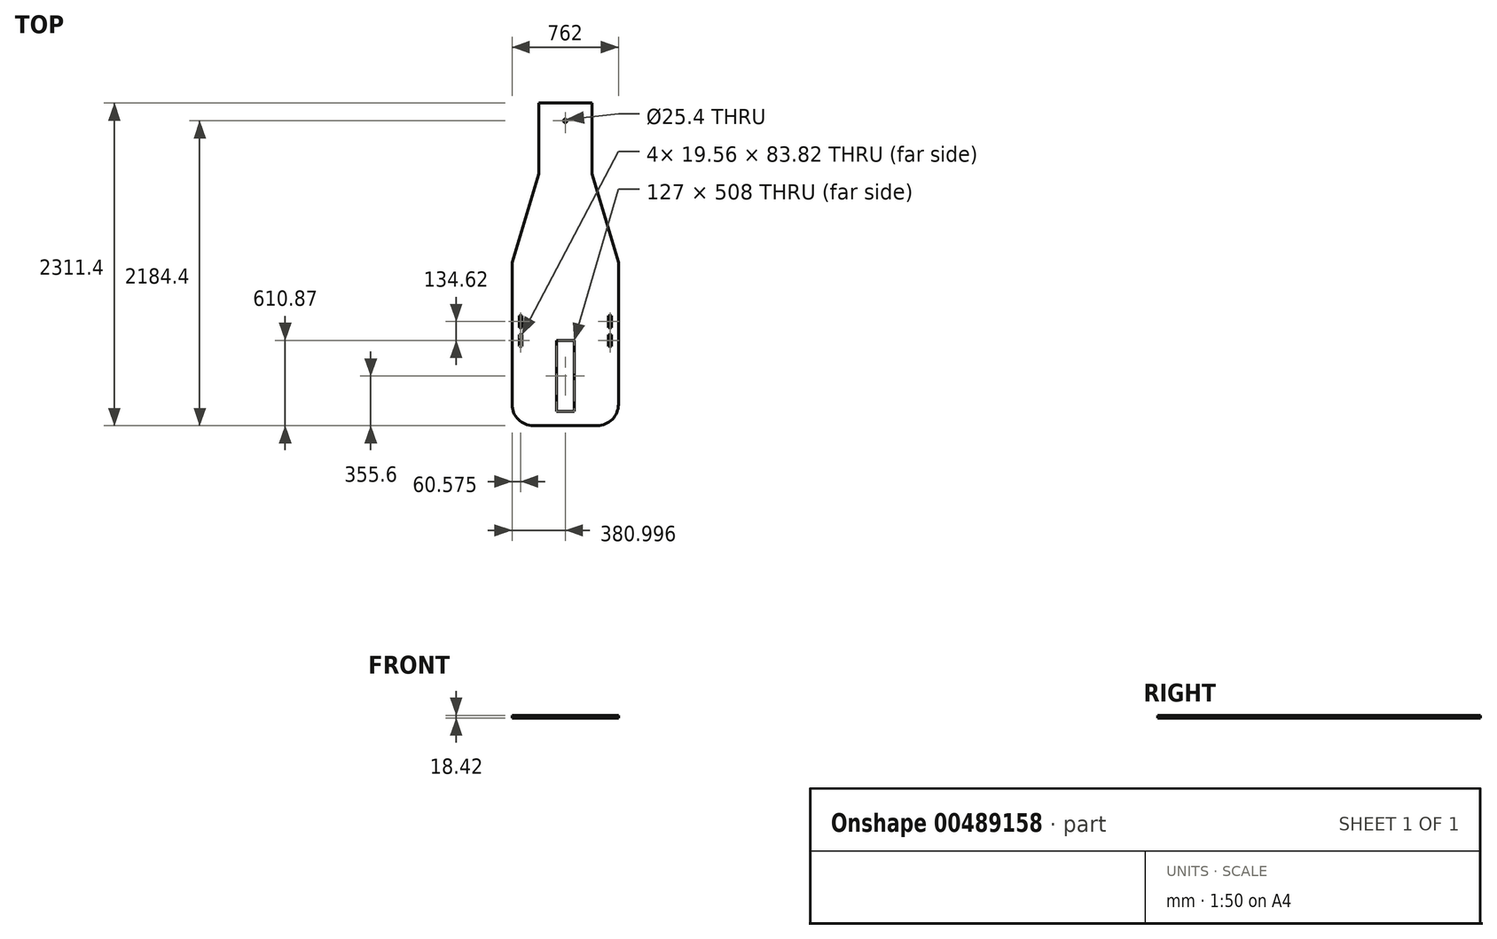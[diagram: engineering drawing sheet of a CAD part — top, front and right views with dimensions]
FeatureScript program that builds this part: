
annotation { "Feature Type Name" : "Feature", "Feature Type Description" : "" }
export const myFeature = defineFeature(function(context is Context, id is Id, definition is map)
    precondition{}
    {
        {
            var Q0;
            Q0=qCreatedBy(makeId("Top.planeOp"),FACE);
            var sketch = newSketch(context, id + "F0", { "sketchPlane" : qUnion([Q0])});
            skLineSegment(sketch, "E0.bottom", {"start": v(158.39, 0) * mm, "end": v(615.59, 0) * mm});
            skLineSegment(sketch, "E1.bottom", {"start": v(323.49, 609.6) * mm, "end": v(450.49, 609.6) * mm});
            skLineSegment(sketch, "E1.top", {"start": v(323.49, 101.6) * mm, "end": v(450.49, 101.6) * mm});
            skLineSegment(sketch, "E1.left", {"start": v(323.49, 609.6) * mm, "end": v(323.49, 101.6) * mm});
            skLineSegment(sketch, "E1.right", {"start": v(450.49, 609.6) * mm, "end": v(450.49, 101.6) * mm});
            skPoint(sketch, "E2.visualSharp", {"position": v(0, 0) * mm});
            skArc(sketch, "E2.filletArc", {"start": v(5.99, 152.4) * mm, "mid": v(50.62, 44.64) * mm, "end": v(158.39, 0) * mm});
            skPoint(sketch, "E3.visualSharp", {"position": v(762, 0) * mm});
            skArc(sketch, "E3.filletArc", {"start": v(615.59, 0) * mm, "mid": v(723.35, 44.64) * mm, "end": v(767.99, 152.4) * mm});
            skLineSegment(sketch, "E4", {"start": v(5.99, 1168.4) * mm, "end": v(196.49, 1803.4) * mm});
            skLineSegment(sketch, "E5", {"start": v(577.49, 1803.4) * mm, "end": v(767.99, 1168.4) * mm});
            skLineSegment(sketch, "E6", {"start": v(767.99, 152.4) * mm, "end": v(767.99, 1168.4) * mm});
            skLineSegment(sketch, "E7", {"start": v(5.99, 152.4) * mm, "end": v(5.99, 1168.4) * mm});
            skLineSegment(sketch, "E8", {"start": v(196.49, 1803.4) * mm, "end": v(196.49, 2311.4) * mm});
            skLineSegment(sketch, "E9", {"start": v(577.49, 2311.4) * mm, "end": v(196.49, 2311.4) * mm});
            skLineSegment(sketch, "E10", {"start": v(577.49, 2311.4) * mm, "end": v(577.49, 1803.4) * mm});
            skLineSegment(sketch, "E11", {"start": v(697.63, 787.4) * mm, "end": v(717.19, 787.4) * mm});
            skLineSegment(sketch, "E12", {"start": v(717.19, 787.4) * mm, "end": v(717.19, 703.58) * mm});
            skLineSegment(sketch, "E13", {"start": v(717.19, 703.58) * mm, "end": v(697.63, 703.58) * mm});
            skLineSegment(sketch, "E14", {"start": v(697.63, 703.58) * mm, "end": v(697.63, 787.4) * mm});
            skLineSegment(sketch, "E15", {"start": v(697.63, 652.78) * mm, "end": v(697.63, 568.96) * mm});
            skLineSegment(sketch, "E16", {"start": v(717.19, 568.96) * mm, "end": v(717.19, 652.78) * mm});
            skLineSegment(sketch, "E17", {"start": v(717.19, 652.78) * mm, "end": v(697.63, 652.78) * mm});
            skLineSegment(sketch, "E18", {"start": v(697.63, 568.96) * mm, "end": v(717.19, 568.96) * mm});
            skLineSegment(sketch, "E19", {"start": v(56.79, 568.96) * mm, "end": v(56.79, 652.78) * mm});
            skLineSegment(sketch, "E20", {"start": v(56.79, 652.78) * mm, "end": v(76.34, 652.78) * mm});
            skLineSegment(sketch, "E21", {"start": v(76.34, 652.78) * mm, "end": v(76.34, 568.96) * mm});
            skLineSegment(sketch, "E22", {"start": v(76.34, 568.96) * mm, "end": v(56.79, 568.96) * mm});
            skLineSegment(sketch, "E23", {"start": v(56.79, 703.58) * mm, "end": v(56.79, 787.4) * mm});
            skLineSegment(sketch, "E24", {"start": v(56.79, 787.4) * mm, "end": v(76.34, 787.4) * mm});
            skLineSegment(sketch, "E25", {"start": v(76.34, 787.4) * mm, "end": v(76.34, 703.58) * mm});
            skLineSegment(sketch, "E26", {"start": v(76.34, 703.58) * mm, "end": v(56.79, 703.58) * mm});
            skCircle(sketch, "E27", {"center": v(386.99, 2184.4) * mm, "radius": 12.7 * mm});
            skSolve(sketch);
        }
        {
            var Q0;
            Q0=makeQuery(id+"F0.imprint","IMPRINT",FACE,{"disambiguationData":[TD([[makeQuery(id+"F0.imprint","IMPRINT",EDGE,{"derivedFrom":sQuery(id+"F0.wireOp",EDGE,"E0.bottom")}),1.0]])]});
            extrude(context, id + "F1", {"entities" : qUnion([Q0]), "depth" : 18.41 * mm, "offsetDistance" : 25.4 * mm});
        }
    });
